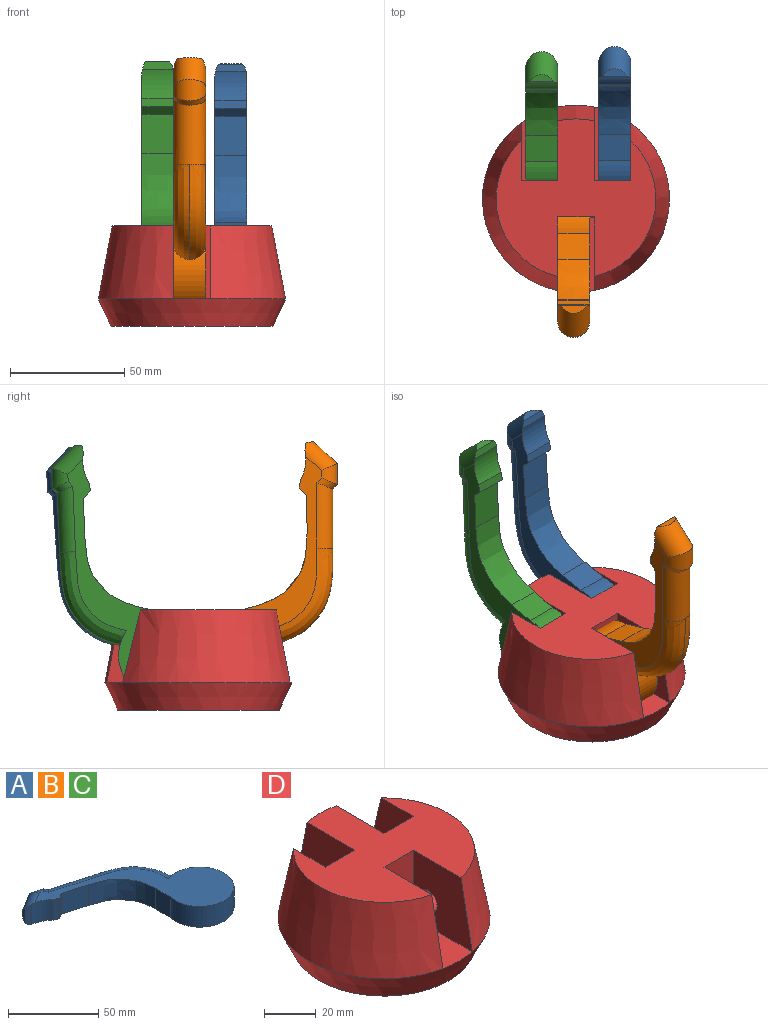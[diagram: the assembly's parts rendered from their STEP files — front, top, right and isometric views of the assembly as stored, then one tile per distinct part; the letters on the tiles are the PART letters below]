
ASSEMBLY  parts=4 mates=3
PART A: 17 faces, bbox 101.6x85.4x14.1 mm
  f0: plane 14x11.66mm, normal (-1,0,0), area 163.3mm2, adj f1,f8,f9,f10
  f1: cylinder r=19mm len=38mm, axis (0,0,-1), area 1369.2mm2, adj f0,f9,f10,f11,f12
  f2: plane 10.72x3.22mm, normal (-0.99,0.14,0), area 24.2mm2, adj f3,f16
  f3: plane 13.65x3.11mm, normal (-0.41,-0.91,0), area 40.8mm2, adj f2,f4,f16
  f4: cylinder r=18.4mm len=14mm, axis (0,0,-1), area 186.7mm2, adj f3,f5,f9,f10,f16
  f5: plane 14x3.4mm, normal (-0.41,-0.91,0), area 52.2mm2, adj f4,f6,f9,f10
  f6: plane 14x3.85mm, normal (0.52,-0.86,0), area 62.9mm2, adj f5,f7,f9,f10
  f7: plane 16.41x14mm, normal (-0.27,-0.96,0), area 238.7mm2, adj f6,f8,f9,f10
  f8: extruded ~28.78x24.16mm, area 574mm2, adj f0,f7,f9,f10
  f9: plane 94.39x77.74mm, normal (0,0,1), area 1751.1mm2, adj f0,f1,f4,f5,f6,f7,f8,f11
  f10: plane 94.39x77.74mm, normal (0,0,-1), area 1751mm2, adj f0,f1,f4,f5,f6,f7,f8,f12
  f11: bspline ~38.64x36.57mm, area 561.3mm2, adj f1,f9,f12,f13
  f12: bspline ~37.33x36.51mm, area 561.3mm2, adj f1,f10,f11,f13
  f13: cylinder r=7mm len=29.59mm, axis (0.96,-0.27,0), area 632.2mm2, adj f9,f10,f11,f12,f14
  f14: cylinder r=7mm len=14mm, axis (0.49,-0.87,0), area 62mm2, adj f9,f10,f13,f15
  f15: cylinder r=7mm len=14mm, axis (0.96,-0.27,0), area 155.8mm2, adj f9,f10,f14,f16
  f16: cylinder r=7mm len=17.51mm, axis (0.85,0.52,0), area 299.9mm2, adj f2,f3,f4,f9,f10,f15
PART B: same geometry as A
PART C: same geometry as A
PART D: 27 faces, bbox 82.1x82.1x44.1 mm
  f0: plane 70x69.07mm, normal (0,0,1), area 2695.4mm2, adj f1,f2,f5,f6,f7,f8,f10,f11
  f1: cone r=41mm half-angle=10.6deg, axis (0,0,-1), area 2776.7mm2, adj f0,f4,f12,f16
  f2: cone r=41mm half-angle=10.6deg, axis (0,0,-1), area 2776.7mm2, adj f0,f4,f6,f11
  f3: plane 71x71mm, normal (0,0,-1), area 3959.2mm2, adj f4
  f4: cone r=35.5mm half-angle=24.6deg, axis (0,0,1), area 3172.5mm2, adj f1,f2,f3,f5,f9,f13,f17
  f5: cone r=41mm half-angle=10.6deg, axis (0,0,-1), area 527.2mm2, adj f0,f4,f8,f14
  f6: plane 32x25.24mm, normal (1,0,0), area 607.1mm2, adj f0,f2,f7,f9,f21
  f7: plane 32x16mm, normal (0,1,0), area 512mm2, adj f0,f6,f8,f9
  f8: plane 32.32x32.11mm, normal (-1,0,0), area 854.1mm2, adj f0,f5,f7,f9,f20
  f9: plane 32.21x16mm, normal (0,0,1), area 470.6mm2, adj f4,f6,f7,f8
  f10: plane 32x16mm, normal (0,-1,0), area 512mm2, adj f0,f11,f12,f13
  f11: plane 32.32x32.11mm, normal (1,0,0), area 854.1mm2, adj f0,f2,f10,f13,f18
  f12: plane 32.32x32.11mm, normal (-1,0,0), area 854.1mm2, adj f0,f1,f10,f13,f23
  f13: plane 33x16mm, normal (0,0,1), area 523.8mm2, adj f4,f10,f11,f12
  f14: plane 32.32x32.11mm, normal (1,0,0), area 854.1mm2, adj f0,f5,f15,f17,f20
  f15: plane 32x16mm, normal (0,1,0), area 512mm2, adj f0,f14,f16,f17
  f16: plane 32x25.24mm, normal (-1,0,0), area 607.1mm2, adj f0,f1,f15,f17,f26
  f17: plane 32.21x16mm, normal (0,0,1), area 470.6mm2, adj f4,f14,f15,f16
  f18: cylinder r=5mm len=17mm, axis (1,0,0), area 534.1mm2, adj f11,f19
  f19: plane 10x10mm, normal (1,0,0), area 78.5mm2, adj f18
  f20: cylinder r=5mm len=16mm, axis (1,0,0), area 502.7mm2, adj f8,f14
  f21: cylinder r=5mm len=10mm, axis (1,0,0), area 31.4mm2, adj f6,f22
  f22: plane 10x10mm, normal (1,0,0), area 78.5mm2, adj f21
  f23: cylinder r=5mm len=17mm, axis (-1,0,0), area 534.1mm2, adj f12,f24
  f24: plane 10x10mm, normal (-1,0,0), area 78.5mm2, adj f23
  f25: plane 10x10mm, normal (-1,0,0), area 78.5mm2, adj f26
  f26: cylinder r=5mm len=10mm, axis (-1,0,0), area 31.4mm2, adj f16,f25
PLACE A rot(axis=(0.1,0.99,0.1),90.6deg) t=(-14.34,17.73,25.68)mm
PLACE B rot(axis=(0.7,-0.1,-0.7),168.7deg) t=(-18.34,-14.27,25.68)mm
PLACE C rot(axis=(0.12,0.99,0.12),90.8deg) t=(-46.34,17.73,25.68)mm
PLACE D t=(-24.34,1.73,1.68)mm fixed
MATE revolute B.f1 <-> D.f18  axis (-1,0,0) through (-32.34,-14.27,25.68)mm
MATE revolute C.f1 <-> D.f20  axis (1,0,0) through (-32.34,17.73,25.68)mm
MATE revolute A.f1 <-> D.f20  axis (1,0,0) through (-0.34,17.73,25.68)mm
